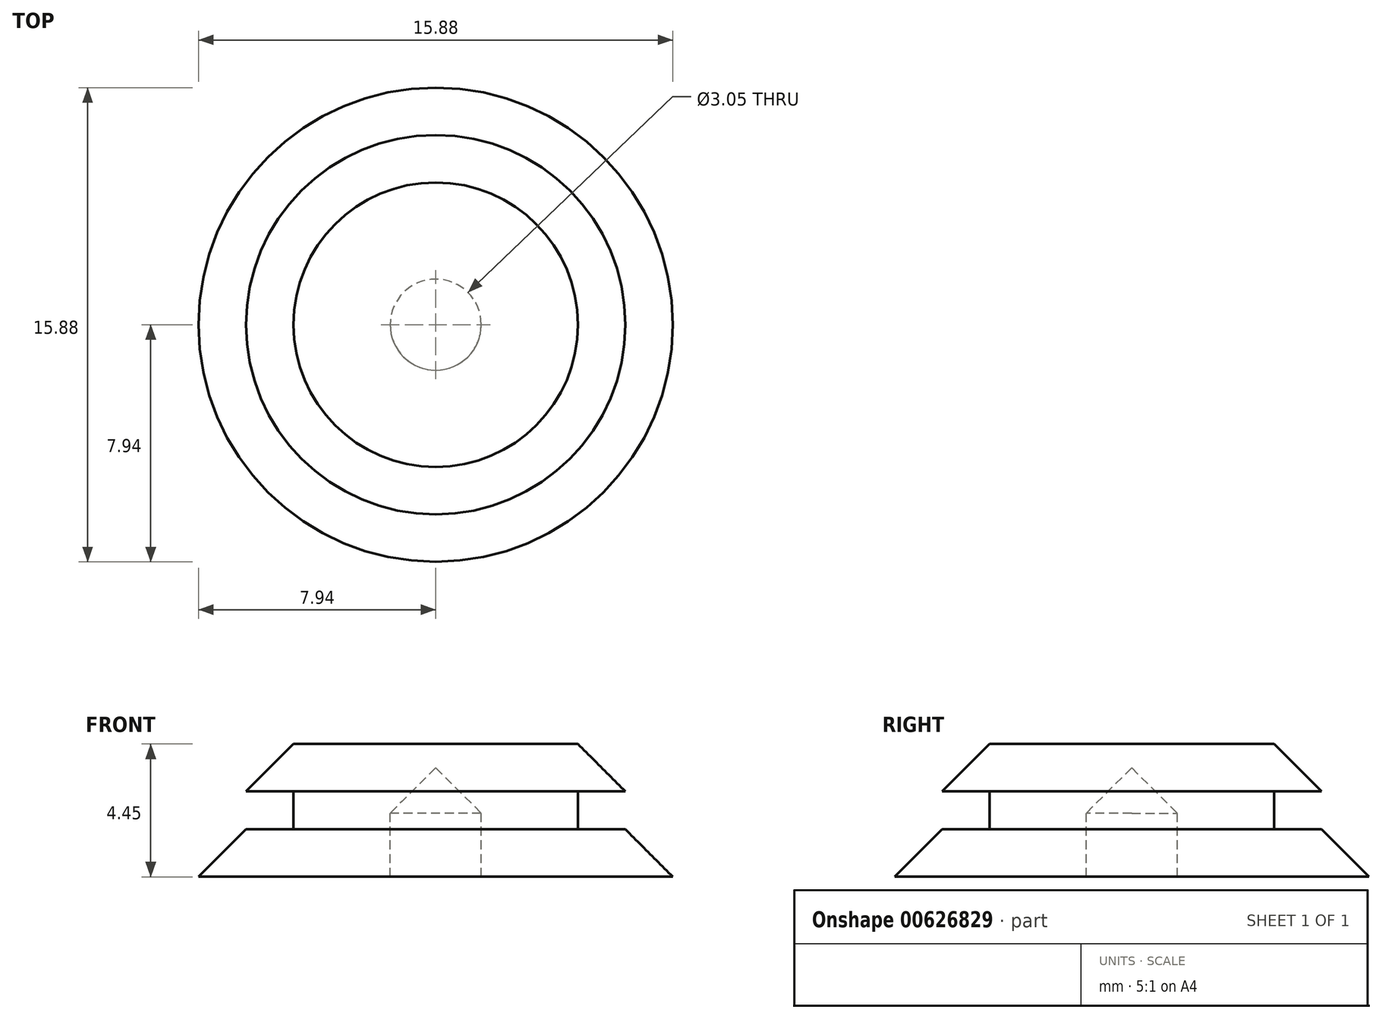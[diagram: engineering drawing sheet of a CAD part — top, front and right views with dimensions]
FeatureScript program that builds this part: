
annotation { "Feature Type Name" : "Feature", "Feature Type Description" : "" }
export const myFeature = defineFeature(function(context is Context, id is Id, definition is map)
    precondition{}
    {
        {
            var Q0;
            Q0=qCreatedBy(makeId("Front.planeOp"),FACE);
            var sketch = newSketch(context, id + "F0", { "sketchPlane" : qUnion([Q0])});
            skLineSegment(sketch, "E0", {"start": v(0, 0) * mm, "end": v(1.59, 1.59) * mm});
            skLineSegment(sketch, "E1", {"start": v(1.59, 1.59) * mm, "end": v(6.35, 1.59) * mm});
            skLineSegment(sketch, "E2", {"start": v(6.35, 1.59) * mm, "end": v(6.35, 0.8) * mm});
            skLineSegment(sketch, "E3", {"start": v(2.7, -2.86) * mm, "end": v(0, -2.86) * mm});
            skLineSegment(sketch, "E4", {"start": v(0, -2.86) * mm, "end": v(0, -1.27) * mm});
            skLineSegment(sketch, "E5", {"start": v(0, -1.27) * mm, "end": v(1.59, -1.27) * mm});
            skLineSegment(sketch, "E6", {"start": v(1.59, -1.27) * mm, "end": v(1.59, 0) * mm});
            skLineSegment(sketch, "E7", {"start": v(1.59, 0) * mm, "end": v(0, 0) * mm});
            skLineSegment(sketch, "E8", {"start": v(6.35, 0.8) * mm, "end": v(2.7, -2.86) * mm});
            skLineSegment(sketch, "E9", {"start": v(0, -1.27) * mm, "end": v(-1.59, -2.86) * mm});
            skLineSegment(sketch, "E10", {"start": v(-1.59, -2.86) * mm, "end": v(0, -2.86) * mm});
            skLineSegment(sketch, "E11", {"start": v(4.83, -0.73) * mm, "end": v(4.83, -2.86) * mm});
            skLineSegment(sketch, "E12", {"start": v(2.7, -2.86) * mm, "end": v(4.83, -2.86) * mm});
            skSolve(sketch);
        }
        {
            var Q0;
            Q0=makeQuery(id+"F0.imprint","IMPRINT",FACE,{"disambiguationData":[TD([[makeQuery(id+"F0.imprint","IMPRINT",EDGE,{"derivedFrom":sQuery(id+"F0.wireOp",EDGE,"E0")}),-1.0]])]});
            var Q1;
            Q1=makeQuery(id+"F0.imprint","IMPRINT",FACE,{"disambiguationData":[TD([[makeQuery(id+"F0.imprint","IMPRINT",EDGE,{"derivedFrom":sQuery(id+"F0.wireOp",EDGE,"E4")}),1.0]])]});
            var Q2;
            {var subQ2=sQuery(id+"F0.wireOp",EDGE,"E11");Q2=makeQuery(id+"F0.imprint","IMPRINT",FACE,{"disambiguationData":[TD([[makeQuery(id+"F0.imprint","IMPRINT",EDGE,{"derivedFrom":subQ2}),-1.0]])]});}
            var Q3;
            Q3=sQuery(id+"F0.wireOp",EDGE,"E2");
            revolve(context, id + "F1", {"entities" : qUnion([Q0, Q1, Q2]), "axis" : qUnion([Q3]), "revolveType" : RevolveType.FULL});
        }
    });
